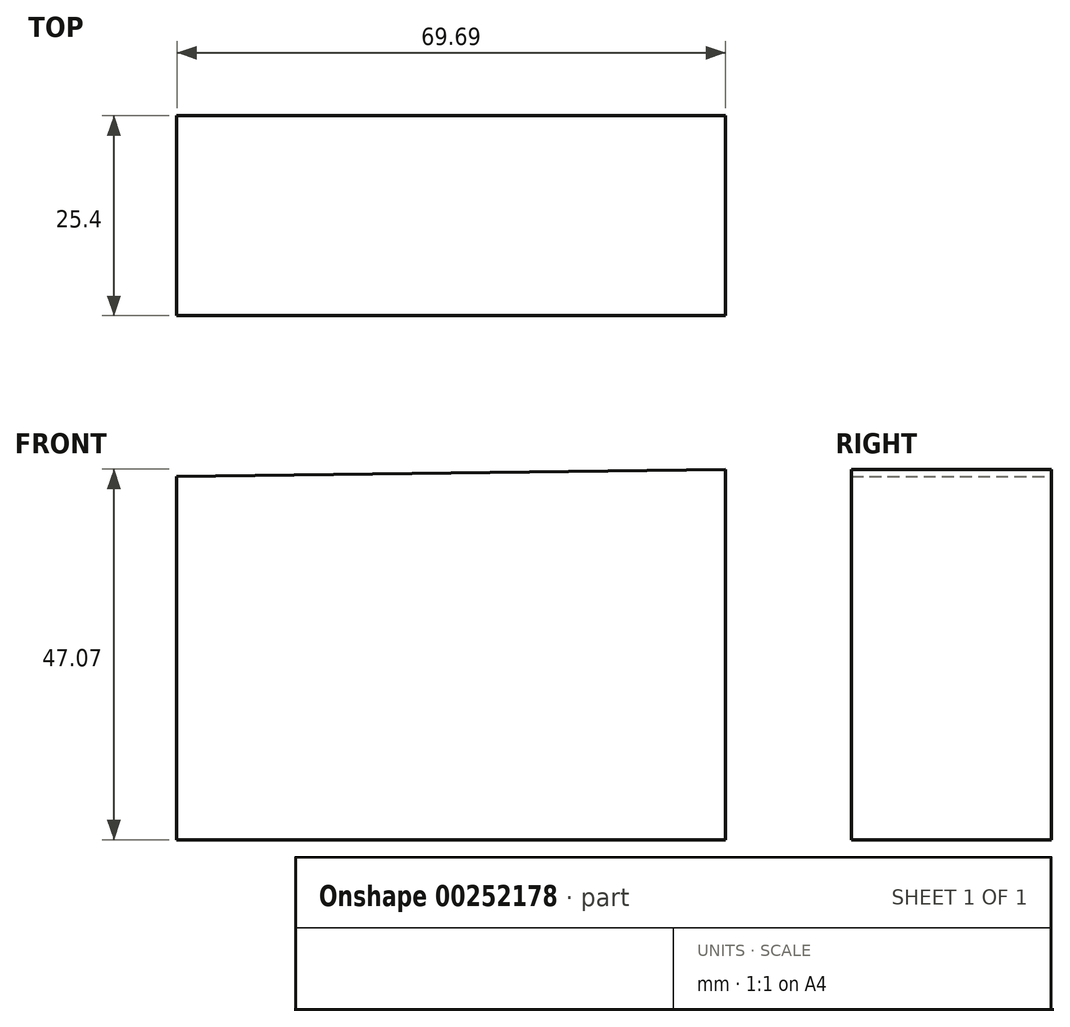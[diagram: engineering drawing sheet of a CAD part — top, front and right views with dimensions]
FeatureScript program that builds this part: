
annotation { "Feature Type Name" : "Feature", "Feature Type Description" : "" }
export const myFeature = defineFeature(function(context is Context, id is Id, definition is map)
    precondition{}
    {
        {
            var Q0;
            Q0=qCreatedBy(makeId("Front.planeOp"),FACE);
            var sketch = newSketch(context, id + "F0", { "sketchPlane" : qUnion([Q0])});
            skLineSegment(sketch, "E0", {"start": v(-111.98, 5.8) * mm, "end": v(-111.98, -40.36) * mm});
            skLineSegment(sketch, "E1", {"start": v(-111.98, -40.36) * mm, "end": v(-42.29, -40.36) * mm});
            skLineSegment(sketch, "E2", {"start": v(-42.29, -40.36) * mm, "end": v(-42.29, 6.7) * mm});
            skLineSegment(sketch, "E3", {"start": v(-42.29, 6.7) * mm, "end": v(-111.98, 5.8) * mm});
            skSolve(sketch);
        }
        {
            var Q0;
            Q0 = qSketchRegion(id + "F0", true);
            extrude(context, id + "F1", {"entities" : qUnion([Q0]), "depth" : 25.4 * mm});
        }
    });
